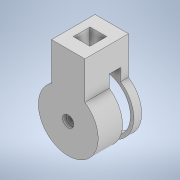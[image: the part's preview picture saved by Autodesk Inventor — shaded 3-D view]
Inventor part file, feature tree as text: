
AUTODESK INVENTOR PART (.ipt)
format: ipt  version: 2022 (Build 260153000, 153)  size: 193,536 bytes
history: native  units: mm
features: extrude x8, sketch x8
ambient origin geometry x8: Origin, YZ Plane, XZ Plane, XY Plane, X Axis, Y Axis, Z Axis, Center Point
bodies: Solid1 (feature_tree)
feature tree (16):
  extrude  "Extrusion1"  Depth=12.0mm TaperAngle=0.0deg
  extrude  "Extrusion2"  Depth=12.0mm TaperAngle=0.0deg
  extrude  "Extrusion3"  Depth=17.2mm TaperAngle=0.0deg
  extrude  "Extrusion4"  Depth=5.0mm TaperAngle=0.0deg
  extrude  "Extrusion5"  Depth=27.0mm TaperAngle=0.0deg
  extrude  "Extrusion6"  Depth=5.0mm TaperAngle=0.0deg
  extrude  "Extrusion7"  Depth=5.0mm
  extrude  "Extrusion8"  [1 undecoded]
  sketch  "Sketch1"  dims[d1=5.0mm d5=12.0mm d6=0.0mm]
  sketch  "Sketch2"  dims[d9=20.0mm d10=12.0mm d11=0.0mm]
  sketch  "Sketch3"  dims[d12=13.0mm d13=17.2mm d14=0.0mm]
  sketch  "Sketch4"  dims[d15=17.0mm d16=5.0mm d17=0.0mm]
  sketch  "Sketch5"  dims[d18=9.0mm d19=27.0mm d20=0.0mm]
  sketch  "Sketch6"  dims[d21=17.0mm d22=5.0mm d23=0.0mm]
  sketch  "Sketch7"  dims[d24=25.4mm d25=0.0mm d30=5.0mm]
  sketch  "Sketch8"  dims[d31=25.4mm d32=0.0mm]
note: 1 required parameter value undecoded (feature->parameter linkage not recoverable at this tier; creation-order binding heuristic only, values carry confidence <= 0.55)
